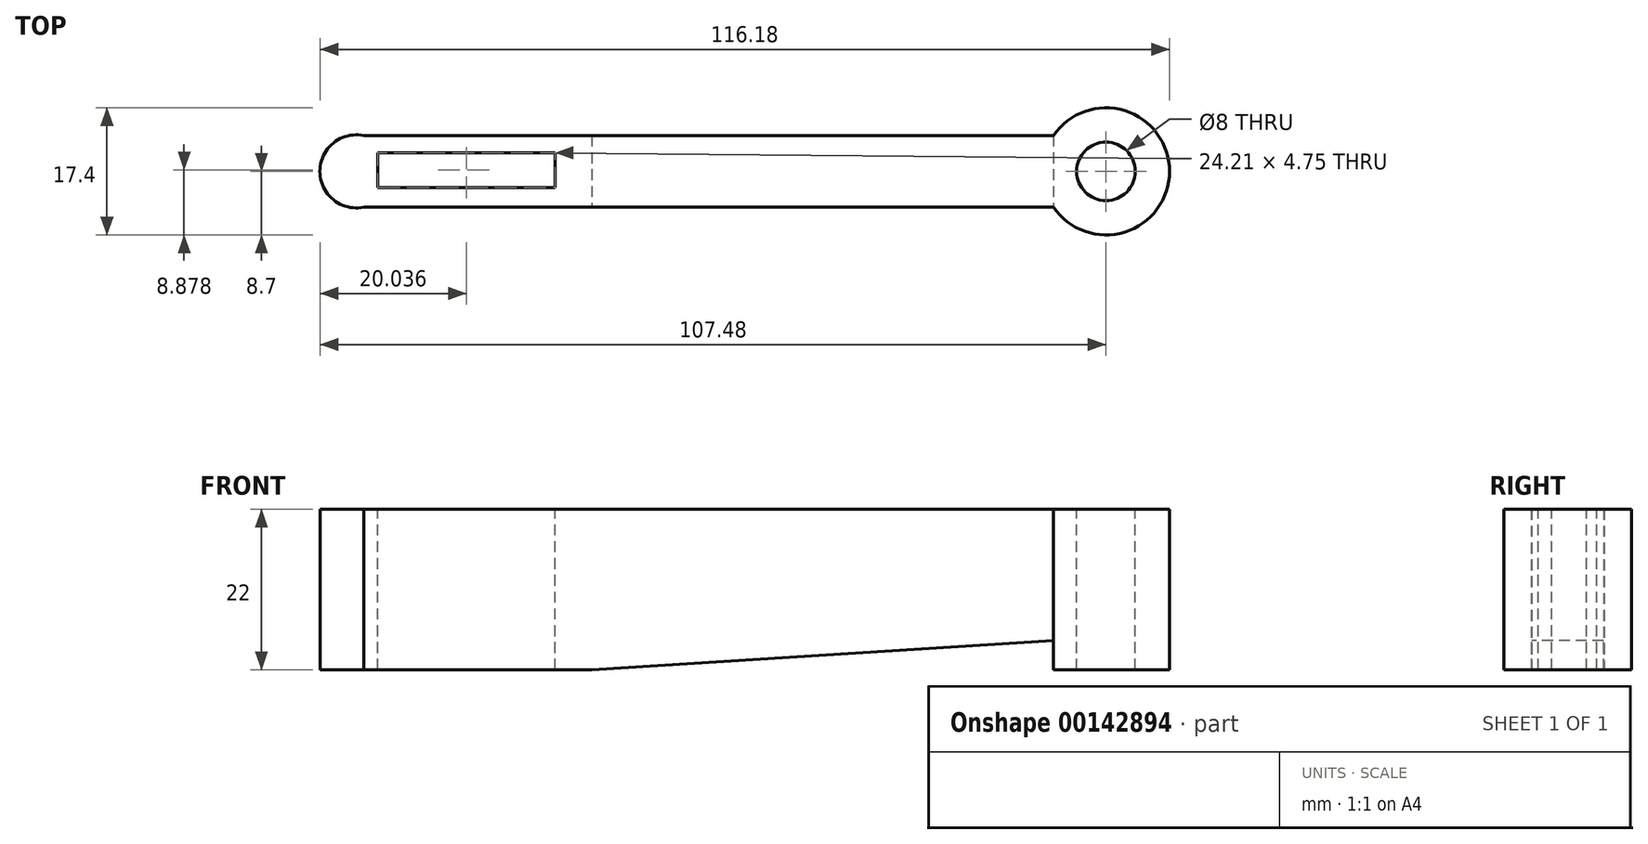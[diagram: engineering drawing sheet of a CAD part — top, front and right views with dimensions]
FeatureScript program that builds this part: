
annotation { "Feature Type Name" : "Feature", "Feature Type Description" : "" }
export const myFeature = defineFeature(function(context is Context, id is Id, definition is map)
    precondition{}
    {
        {
            var Q0;
            Q0=qCreatedBy(makeId("Top.planeOp"),FACE);
            var sketch = newSketch(context, id + "F0", { "sketchPlane" : qUnion([Q0])});
            skArc(sketch, "E0", {"start": v(-7.2, -4.9) * mm, "mid": v(8.7, 0) * mm, "end": v(-7.2, 4.9) * mm});
            skLineSegment(sketch, "E1", {"start": v(-7.2, 4.9) * mm, "end": v(-101.48, 4.9) * mm});
            skLineSegment(sketch, "E2", {"start": v(-7.2, -4.9) * mm, "end": v(-101.48, -4.9) * mm});
            skArc(sketch, "E3", {"start": v(-101.48, 4.9) * mm, "mid": v(-107.48, 0) * mm, "end": v(-101.48, -4.9) * mm});
            skSolve(sketch);
        }
        {
            var Q0;
            Q0 = qSketchRegion(id + "F0", true);
            extrude(context, id + "F1", {"entities" : qUnion([Q0]), "depth" : 22 * mm});
        }
        {
            var Q0;
            Q0=makeQuery(id+"F1.opExtrude","SWEPT_FACE",FACE,{"disambiguationData":[OSD([sQuery(id+"F0.wireOp",EDGE,"E2")])]});
            var sketch = newSketch(context, id + "F2", { "sketchPlane" : qUnion([Q0])});
            skLineSegment(sketch, "E4", {"start": v(-70.33, 0) * mm, "end": v(-7.2, 4) * mm});
            skSolve(sketch);
        }
        {
            var Q0;
            {var subQ0=sQuery(id+"F2.wireOp",EDGE,"E4");Q0=makeQuery(id+"F2.imprint","IMPRINT",FACE,{"disambiguationData":[TD([[makeQuery(id+"F2.imprint","IMPRINT",EDGE,{"derivedFrom":subQ0}),-1.0]])]});}
            extrude(context, id + "F3", {"entities" : qUnion([Q0]), "operationType" : NewBodyOperationType.REMOVE, "endBound" : BoundingType.THROUGH_ALL, "oppositeDirection" : true, "depth" : 25 * mm});
        }
        {
            var Q0;
            Q0=makeQuery(id+"F1.opExtrude","CAP_FACE",FACE,{"disambiguationData":[OSD([sQuery(id+"F0.wireOp",EDGE,"E0"),sQuery(id+"F0.wireOp",EDGE,"E1"),sQuery(id+"F0.wireOp",EDGE,"E2"),sQuery(id+"F0.wireOp",EDGE,"E3")])],"isStart":false});
            var sketch = newSketch(context, id + "F4", { "sketchPlane" : qUnion([Q0])});
            skLineSegment(sketch, "E5.bottom", {"start": v(-99.55, 0) * mm, "end": v(-75.34, 0) * mm});
            skLineSegment(sketch, "E5.top", {"start": v(-99.55, 2.55) * mm, "end": v(-75.34, 2.55) * mm});
            skLineSegment(sketch, "E5.left", {"start": v(-99.55, 0) * mm, "end": v(-99.55, 2.55) * mm});
            skLineSegment(sketch, "E5.right", {"start": v(-75.34, 0) * mm, "end": v(-75.34, 2.55) * mm});
            skLineSegment(sketch, "E6.top", {"start": v(-99.55, -2.2) * mm, "end": v(-75.34, -2.2) * mm});
            skLineSegment(sketch, "E6.left", {"start": v(-99.55, 0) * mm, "end": v(-99.55, -2.2) * mm});
            skLineSegment(sketch, "E6.right", {"start": v(-75.34, 0) * mm, "end": v(-75.34, -2.2) * mm});
            skSolve(sketch);
        }
        {
            var Q0;
            Q0 = qSketchRegion(id + "F4", true);
            extrude(context, id + "F5", {"entities" : qUnion([Q0]), "operationType" : NewBodyOperationType.REMOVE, "endBound" : BoundingType.THROUGH_ALL, "oppositeDirection" : true, "depth" : 25 * mm});
        }
        {
            var Q0;
            Q0=makeQuery(id+"F1.opExtrude","CAP_FACE",FACE,{"disambiguationData":[OSD([sQuery(id+"F0.wireOp",EDGE,"E0"),sQuery(id+"F0.wireOp",EDGE,"E1"),sQuery(id+"F0.wireOp",EDGE,"E2"),sQuery(id+"F0.wireOp",EDGE,"E3")])],"isStart":false});
            var sketch = newSketch(context, id + "F6", { "sketchPlane" : qUnion([Q0])});
            skCircle(sketch, "E7", {"center": v(0, 0) * mm, "radius": 4 * mm});
            skSolve(sketch);
        }
        {
            var Q0;
            Q0 = qSketchRegion(id + "F6", true);
            extrude(context, id + "F7", {"entities" : qUnion([Q0]), "operationType" : NewBodyOperationType.REMOVE, "endBound" : BoundingType.THROUGH_ALL, "oppositeDirection" : true, "depth" : 25 * mm});
        }
    });
